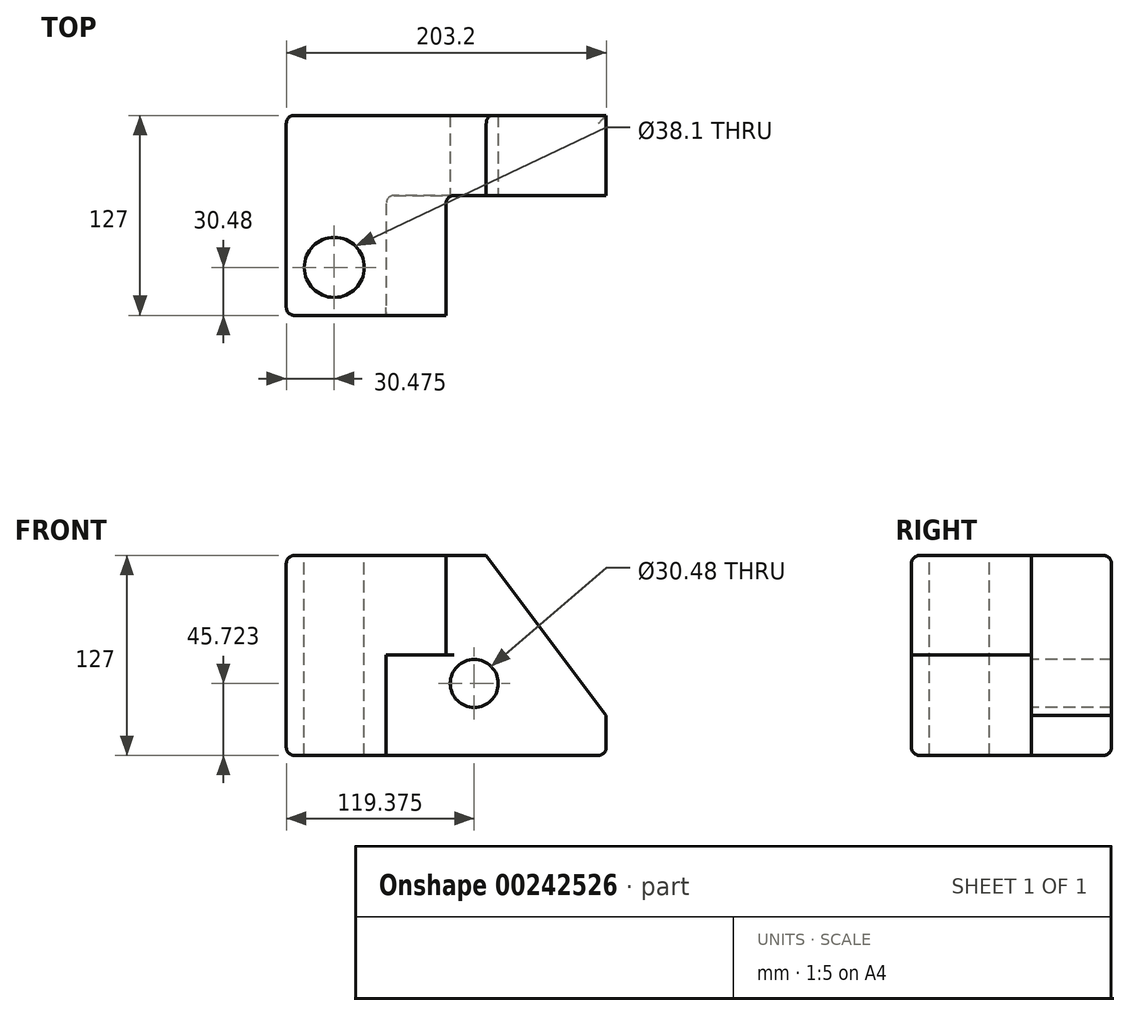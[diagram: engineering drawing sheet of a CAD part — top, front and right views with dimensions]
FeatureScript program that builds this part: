
annotation { "Feature Type Name" : "Feature", "Feature Type Description" : "" }
export const myFeature = defineFeature(function(context is Context, id is Id, definition is map)
    precondition{}
    {
        {
            var Q0;
            Q0=qCreatedBy(makeId("Front.planeOp"),FACE);
            var sketch = newSketch(context, id + "F0", { "sketchPlane" : qUnion([Q0])});
            skLineSegment(sketch, "E0.bottom", {"start": v(101.79, 63.15) * mm, "end": v(-101.41, 63.15) * mm});
            skLineSegment(sketch, "E0.top", {"start": v(101.79, -63.85) * mm, "end": v(-101.41, -63.85) * mm});
            skLineSegment(sketch, "E0.left", {"start": v(101.79, 63.15) * mm, "end": v(101.79, -63.85) * mm});
            skLineSegment(sketch, "E0.right", {"start": v(-101.41, 63.15) * mm, "end": v(-101.41, -63.85) * mm});
            skPoint(sketch, "E0.middle", {"position": v(0.19, -0.35) * mm});
            skSolve(sketch);
        }
        {
            var Q0;
            Q0=makeQuery(id+"F0.imprint","IMPRINT",FACE,{"disambiguationData":[TD([[makeQuery(id+"F0.imprint","IMPRINT",EDGE,{"derivedFrom":sQuery(id+"F0.wireOp",EDGE,"E0.bottom")}),1.0]])]});
            extrude(context, id + "F1", {"entities" : qUnion([Q0]), "depth" : 127 * mm});
        }
        {
            var Q0;
            Q0=makeQuery(id+"F1.opExtrude","CAP_FACE",FACE,{"disambiguationData":[OSD([sQuery(id+"F0.wireOp",EDGE,"E0.bottom"),sQuery(id+"F0.wireOp",EDGE,"E0.top"),sQuery(id+"F0.wireOp",EDGE,"E0.left"),sQuery(id+"F0.wireOp",EDGE,"E0.right")])],"isStart":false});
            var sketch = newSketch(context, id + "F2", { "sketchPlane" : qUnion([Q0])});
            skLineSegment(sketch, "E1", {"start": v(-101.41, 63.15) * mm, "end": v(0, 63.15) * mm});
            skLineSegment(sketch, "E2", {"start": v(-101.41, 63.15) * mm, "end": v(-101.41, -63.85) * mm});
            skLineSegment(sketch, "E3", {"start": v(-101.41, -63.85) * mm, "end": v(-37.91, -63.85) * mm});
            skLineSegment(sketch, "E4", {"start": v(-37.91, -63.85) * mm, "end": v(-37.91, 0) * mm});
            skLineSegment(sketch, "E5", {"start": v(-37.91, 0) * mm, "end": v(0, 0) * mm});
            skLineSegment(sketch, "E6", {"start": v(0, 0) * mm, "end": v(0, 63.15) * mm});
            skSolve(sketch);
        }
        {
            var Q0;
            {var subQ3=sQuery(id+"F2.wireOp",EDGE,"E4");Q0=makeQuery(id+"F2.imprint","IMPRINT",FACE,{"disambiguationData":[TD([[makeQuery(id+"F2.imprint","IMPRINT",EDGE,{"derivedFrom":subQ3}),-1.0]])]});}
            extrude(context, id + "F3", {"entities" : qUnion([Q0]), "operationType" : NewBodyOperationType.REMOVE, "oppositeDirection" : true, "depth" : 76.2 * mm});
        }
        {
            var Q0;
            Q0=makeQuery(id+"F1.opExtrude","SWEPT_EDGE",EDGE,{"disambiguationData":[OSD([sQuery(id+"F0.wireOp",EDGE,"E0.bottom"),sQuery(id+"F0.wireOp",EDGE,"E0.left")])]});
            chamfer(context, id + "F4", {"entities" : qUnion([Q0]), "chamferType" : ChamferType.TWO_OFFSETS, "width1" : 76.2 * mm, "oppositeDirection" : false, "width2" : 101.6 * mm, "tangentPropagation" : true});
        }
        {
            var Q0;
            Q0=makeQuery(id+"F1.opExtrude","CAP_EDGE",EDGE,{"disambiguationData":[OSD([sQuery(id+"F0.wireOp",EDGE,"E0.bottom")])],"isStart":false});
            var Q1;
            Q1=makeQuery(id+"F3.boolean.opBoolean","COPY",EDGE,{"derivedFrom":makeQuery(id+"F3.opExtrude","SWEPT_EDGE",EDGE,{"disambiguationData":[OSD([sQuery(id+"F0.wireOp",EDGE,"E0.bottom"),sQuery(id+"F2.wireOp",EDGE,"E1"),sQuery(id+"F2.wireOp",EDGE,"E6")])]})});
            var Q2;
            Q2=makeQuery(id+"F3.boolean.opBoolean","COPY",EDGE,{"derivedFrom":makeQuery(id+"F3.opExtrude","CAP_EDGE",EDGE,{"disambiguationData":[OSD([sQuery(id+"F2.wireOp",EDGE,"E6")])],"isStart":true})});
            var Q3;
            Q3=makeQuery(id+"F3.boolean.opBoolean","COPY",EDGE,{"derivedFrom":makeQuery(id+"F3.opExtrude","CAP_EDGE",EDGE,{"disambiguationData":[OSD([sQuery(id+"F2.wireOp",EDGE,"E5")])],"isStart":true})});
            var Q4;
            Q4=makeQuery(id+"F3.boolean.opBoolean","COPY",EDGE,{"derivedFrom":makeQuery(id+"F3.opExtrude","CAP_EDGE",EDGE,{"disambiguationData":[OSD([sQuery(id+"F2.wireOp",EDGE,"E4")])],"isStart":true})});
            var Q5;
            Q5=makeQuery(id+"F3.boolean.opBoolean","COPY",EDGE,{"derivedFrom":makeQuery(id+"F3.opExtrude","CAP_EDGE",EDGE,{"disambiguationData":[OSD([sQuery(id+"F2.wireOp",EDGE,"E4")])],"isStart":false})});
            var Q6;
            Q6=makeQuery(id+"F3.boolean.opBoolean","COPY",EDGE,{"derivedFrom":makeQuery(id+"F3.opExtrude","CAP_EDGE",EDGE,{"disambiguationData":[OSD([sQuery(id+"F0.wireOp",EDGE,"E0.bottom")])],"isStart":false})});
            var Q7;
            Q7=makeQuery(id+"F3.boolean.opBoolean","COPY",EDGE,{"derivedFrom":makeQuery(id+"F3.opExtrude","CAP_EDGE",EDGE,{"disambiguationData":[OSD([sQuery(id+"F2.wireOp",EDGE,"E6")])],"isStart":false})});
            var Q8;
            Q8=makeQuery(id+"F1.opExtrude","CAP_EDGE",EDGE,{"disambiguationData":[OSD([sQuery(id+"F0.wireOp",EDGE,"E0.bottom")])],"isStart":true});
            var Q9;
            Q9=makeQuery(id+"F1.opExtrude","SWEPT_EDGE",EDGE,{"disambiguationData":[OSD([sQuery(id+"F0.wireOp",EDGE,"E0.bottom"),sQuery(id+"F0.wireOp",EDGE,"E0.right")])]});
            var Q10;
            Q10=makeQuery(id+"F1.opExtrude","CAP_EDGE",EDGE,{"disambiguationData":[OSD([sQuery(id+"F0.wireOp",EDGE,"E0.right")])],"isStart":false});
            var Q11;
            Q11=makeQuery(id+"F1.opExtrude","CAP_EDGE",EDGE,{"disambiguationData":[OSD([sQuery(id+"F0.wireOp",EDGE,"E0.right")])],"isStart":true});
            var Q12;
            Q12=makeQuery(id+"F1.opExtrude","CAP_EDGE",EDGE,{"disambiguationData":[OSD([sQuery(id+"F0.wireOp",EDGE,"E0.top")])],"isStart":false});
            var Q13;
            Q13=makeQuery(id+"F3.boolean.opBoolean","COPY",EDGE,{"derivedFrom":makeQuery(id+"F3.opExtrude","SWEPT_EDGE",EDGE,{"disambiguationData":[OSD([sQuery(id+"F0.wireOp",EDGE,"E0.top"),sQuery(id+"F2.wireOp",EDGE,"E3"),sQuery(id+"F2.wireOp",EDGE,"E4")])]})});
            var Q14;
            Q14=makeQuery(id+"F1.opExtrude","SWEPT_EDGE",EDGE,{"disambiguationData":[OSD([sQuery(id+"F0.wireOp",EDGE,"E0.top"),sQuery(id+"F0.wireOp",EDGE,"E0.left")])]});
            var Q15;
            Q15=makeQuery(id+"F1.opExtrude","CAP_EDGE",EDGE,{"disambiguationData":[OSD([sQuery(id+"F0.wireOp",EDGE,"E0.top")])],"isStart":true});
            var Q16;
            Q16=makeQuery(id+"F1.opExtrude","SWEPT_EDGE",EDGE,{"disambiguationData":[OSD([sQuery(id+"F0.wireOp",EDGE,"E0.top"),sQuery(id+"F0.wireOp",EDGE,"E0.right")])]});
            fillet(context, id + "F5", {"entities" : qUnion([Q0, Q1, Q2, Q3, Q4, Q5, Q6, Q7, Q8, Q9, Q10, Q11, Q12, Q13, Q14, Q15, Q16]), "radius" : 5.08 * mm, "tangentPropagation" : true, "allowEdgeOverflow" : false});
        }
        {
            var Q0;
            Q0=makeQuery(id+"F3.boolean.opBoolean","COPY",FACE,{"derivedFrom":makeQuery(id+"F3.opExtrude","CAP_FACE",FACE,{"disambiguationData":[OSD([sQuery(id+"F0.wireOp",EDGE,"E0.bottom"),sQuery(id+"F0.wireOp",EDGE,"E0.top"),sQuery(id+"F0.wireOp",EDGE,"E0.left"),sQuery(id+"F2.wireOp",EDGE,"E4"),sQuery(id+"F2.wireOp",EDGE,"E5"),sQuery(id+"F2.wireOp",EDGE,"E6")])],"isStart":false})});
            var sketch = newSketch(context, id + "F6", { "sketchPlane" : qUnion([Q0])});
            skCircle(sketch, "E7", {"center": v(17.97, -18.13) * mm, "radius": 15.24 * mm});
            skSolve(sketch);
        }
        {
            var Q0;
            Q0=makeQuery(id+"F6.imprint","IMPRINT",FACE,{"disambiguationData":[TD([[makeQuery(id+"F6.imprint","IMPRINT",EDGE,{"derivedFrom":sQuery(id+"F6.wireOp",EDGE,"E7")}),1.0]])]});
            var Q1;
            Q1=makeQuery(id+"F1.opExtrude","CAP_FACE",FACE,{"disambiguationData":[OSD([sQuery(id+"F0.wireOp",EDGE,"E0.bottom"),sQuery(id+"F0.wireOp",EDGE,"E0.top"),sQuery(id+"F0.wireOp",EDGE,"E0.left"),sQuery(id+"F0.wireOp",EDGE,"E0.right")])],"isStart":true});
            extrude(context, id + "F7", {"entities" : qUnion([Q0]), "operationType" : NewBodyOperationType.REMOVE, "endBound" : BoundingType.UP_TO_SURFACE, "oppositeDirection" : true, "endBoundEntityFace" : qUnion([Q1]), "depth" : 25.4 * mm});
        }
        {
            var Q0;
            Q0=makeQuery(id+"F1.opExtrude","SWEPT_FACE",FACE,{"disambiguationData":[OSD([sQuery(id+"F0.wireOp",EDGE,"E0.bottom")])]});
            var sketch = newSketch(context, id + "F8", { "sketchPlane" : qUnion([Q0])});
            skCircle(sketch, "E8", {"center": v(-70.93, -96.52) * mm, "radius": 19.05 * mm});
            skSolve(sketch);
        }
        {
            var Q0;
            Q0=makeQuery(id+"F8.imprint","IMPRINT",FACE,{"disambiguationData":[TD([[makeQuery(id+"F8.imprint","IMPRINT",EDGE,{"derivedFrom":sQuery(id+"F8.wireOp",EDGE,"E8")}),1.0]])]});
            var Q1;
            Q1=makeQuery(id+"F1.opExtrude","SWEPT_FACE",FACE,{"disambiguationData":[OSD([sQuery(id+"F0.wireOp",EDGE,"E0.top")])]});
            extrude(context, id + "F9", {"entities" : qUnion([Q0]), "operationType" : NewBodyOperationType.REMOVE, "endBound" : BoundingType.UP_TO_SURFACE, "oppositeDirection" : true, "endBoundEntityFace" : qUnion([Q1]), "depth" : 25.4 * mm});
        }
    });
